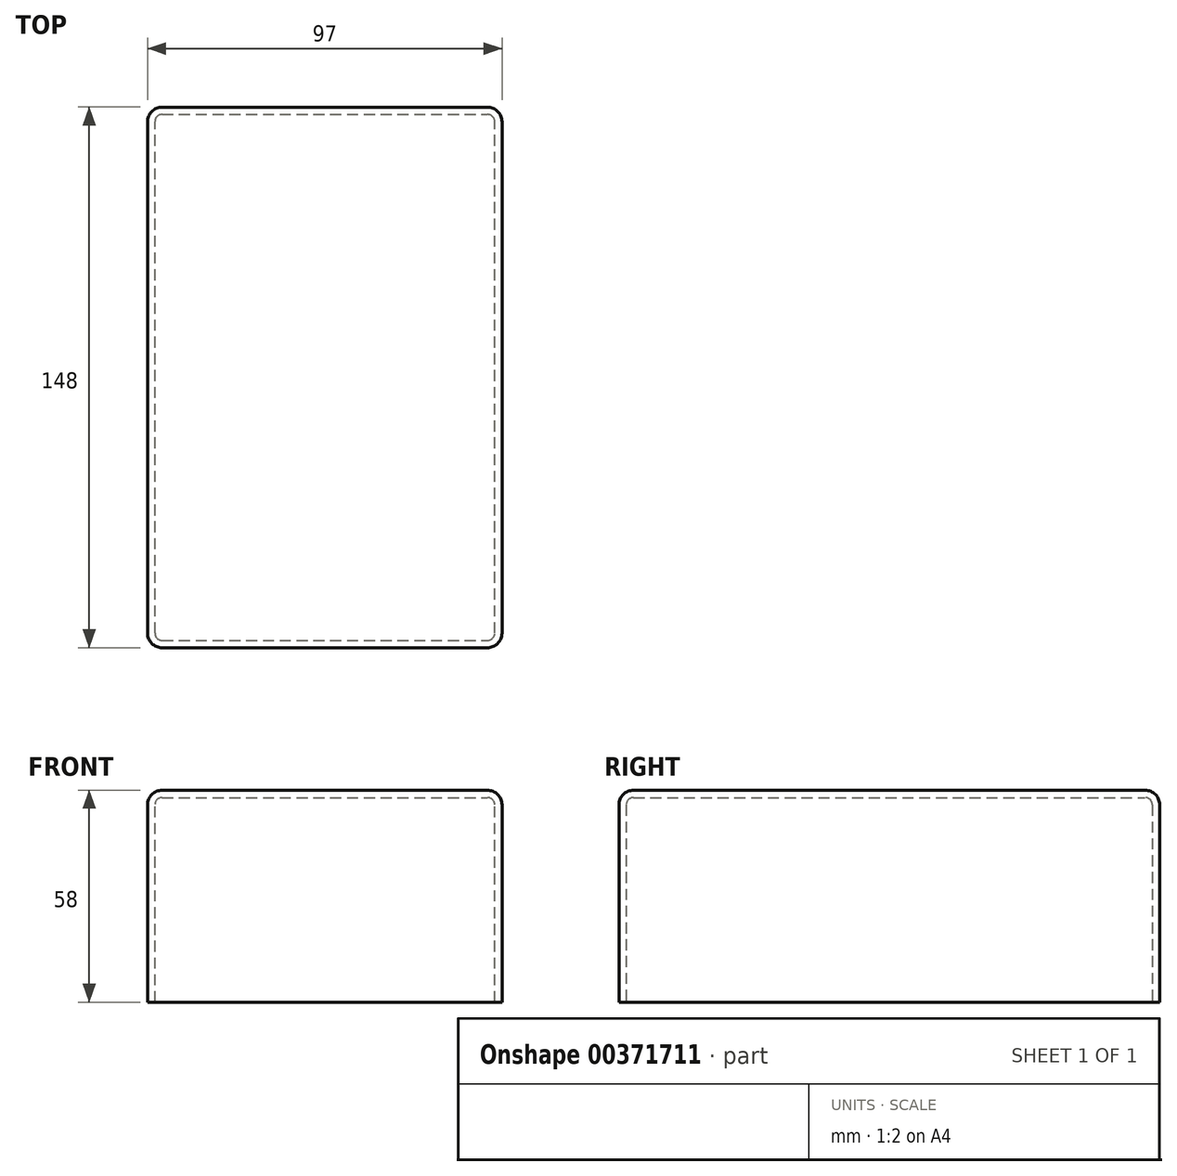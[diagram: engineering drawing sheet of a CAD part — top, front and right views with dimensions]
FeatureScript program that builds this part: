
annotation { "Feature Type Name" : "Feature", "Feature Type Description" : "" }
export const myFeature = defineFeature(function(context is Context, id is Id, definition is map)
    precondition{}
    {
        {
            var Q0;
            Q0=qCreatedBy(makeId("Front.planeOp"),FACE);
            var sketch = newSketch(context, id + "F0", { "sketchPlane" : qUnion([Q0])});
            skLineSegment(sketch, "E0.bottom", {"start": v(70, 29) * mm, "end": v(-70, 29) * mm});
            skLineSegment(sketch, "E0.top", {"start": v(74, -29) * mm, "end": v(-74, -29) * mm});
            skLineSegment(sketch, "E0.left", {"start": v(74, 25) * mm, "end": v(74, -29) * mm});
            skLineSegment(sketch, "E0.right", {"start": v(-74, 25) * mm, "end": v(-74, -29) * mm});
            skPoint(sketch, "E0.middle", {"position": v(0, 0) * mm});
            skPoint(sketch, "E1.visualSharp", {"position": v(-74, 29) * mm});
            skArc(sketch, "E1.filletArc", {"start": v(-70, 29) * mm, "mid": v(-72.83, 27.83) * mm, "end": v(-74, 25) * mm});
            skPoint(sketch, "E2.visualSharp", {"position": v(74, 29) * mm});
            skArc(sketch, "E2.filletArc", {"start": v(74, 25) * mm, "mid": v(72.83, 27.83) * mm, "end": v(70, 29) * mm});
            skSolve(sketch);
        }
        {
            var Q0;
            Q0=makeQuery(id+"F0.imprint","IMPRINT",FACE,{"disambiguationData":[TD([[makeQuery(id+"F0.imprint","IMPRINT",EDGE,{"derivedFrom":sQuery(id+"F0.wireOp",EDGE,"E0.bottom")}),1.0]])]});
            extrude(context, id + "F1", {"entities" : qUnion([Q0]), "endBound" : BoundingType.SYMMETRIC, "depth" : 97 * mm});
        }
        {
            var Q0;
            Q0=makeQuery(id+"F1.opExtrude","CAP_EDGE",EDGE,{"disambiguationData":[OSD([sQuery(id+"F0.wireOp",EDGE,"E2.filletArc")])],"isStart":false});
            fillet(context, id + "F2", {"entities" : qUnion([Q0]), "radius" : 4 * mm, "tangentPropagation" : true, "allowEdgeOverflow" : false});
        }
        {
            var Q0;
            Q0=makeQuery(id+"F1.opExtrude","CAP_EDGE",EDGE,{"disambiguationData":[OSD([sQuery(id+"F0.wireOp",EDGE,"E2.filletArc")])],"isStart":true});
            var Q1;
            Q1=makeQuery(id+"F1.opExtrude","SWEPT_EDGE",EDGE,{"disambiguationData":[OSD([sQuery(id+"F0.wireOp",EDGE,"E0.bottom"),sQuery(id+"F0.wireOp",EDGE,"E2.filletArc")])]});
            fillet(context, id + "F3", {"entities" : qUnion([Q0, Q1]), "radius" : 4 * mm, "tangentPropagation" : true, "allowEdgeOverflow" : false});
        }
        {
            var Q0;
            Q0=makeQuery(id+"F1.opExtrude","SWEPT_FACE",FACE,{"disambiguationData":[OSD([sQuery(id+"F0.wireOp",EDGE,"E0.top")])]});
            shell(context, id + "F4", {"entities" : qUnion([Q0]), "thickness" : 2 * mm});
        }
        {
            var Q0;
            Q0=makeQuery(id+"F1.opExtrude","SWEPT_BODY",BODY,{"disambiguationData":[OSD([sQuery(id+"F0.wireOp",EDGE,"E0.bottom"),sQuery(id+"F0.wireOp",EDGE,"E0.top"),sQuery(id+"F0.wireOp",EDGE,"E0.left"),sQuery(id+"F0.wireOp",EDGE,"E0.right"),sQuery(id+"F0.wireOp",EDGE,"E1.filletArc"),sQuery(id+"F0.wireOp",EDGE,"E2.filletArc")])]});
            var Q1;
            {var subQ0=sQuery(id+"F0.wireOp",EDGE,"E0.left");Q1=makeQuery(id+"F2.opFillet","BLEND_EDGE",EDGE,{"blendedFrom":[makeQuery(id+"F1.opExtrude","CAP_EDGE",EDGE,{"disambiguationData":[OSD([subQ0])],"isStart":false}),makeQuery(id+"F1.opExtrude","SWEPT_FACE",FACE,{"disambiguationData":[OSD([subQ0])]})],"blendedInto":[makeQuery(id+"F1.opExtrude","SWEPT_FACE",FACE,{"disambiguationData":[OSD([subQ0])]})]});}
            transform(context, id + "F5", {"entities" : qUnion([Q0]), "transformType" : TransformType.ROTATION, "transformAxis" : qUnion([Q1]), "angle" : 90 * degree, "makeCopy" : false});
        }
        {
            var Q0;
            Q0=makeQuery(id+"F1.opExtrude","SWEPT_BODY",BODY,{"disambiguationData":[OSD([sQuery(id+"F0.wireOp",EDGE,"E0.bottom"),sQuery(id+"F0.wireOp",EDGE,"E0.top"),sQuery(id+"F0.wireOp",EDGE,"E0.left"),sQuery(id+"F0.wireOp",EDGE,"E0.right"),sQuery(id+"F0.wireOp",EDGE,"E1.filletArc"),sQuery(id+"F0.wireOp",EDGE,"E2.filletArc")])]});
            transform(context, id + "F6", {"entities" : qUnion([Q0]), "transformType" : TransformType.TRANSLATION_3D, "dx" : -118.36 * mm, "dy" : -29.46 * mm, "dz" : 0 * mm, "makeCopy" : false});
        }
    });
